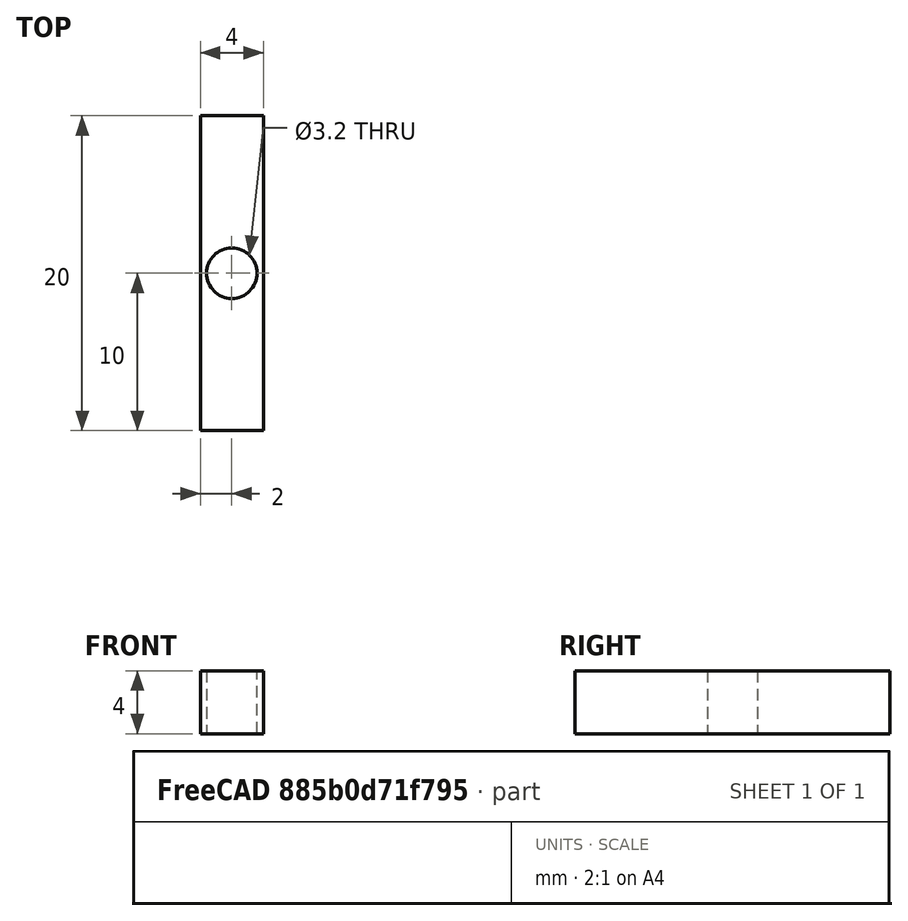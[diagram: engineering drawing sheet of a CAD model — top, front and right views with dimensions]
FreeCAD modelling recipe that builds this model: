
FCSTD DOCUMENT  (FreeCAD 0.18R14090 (Git))
Label: XEndStopClip3
License: All rights reserved
LicenseURL: http://en.wikipedia.org/wiki/All_rights_reserved
objects: Sketcher::SketchObject×1, PartDesign::Pad×1, PartDesign::Body×1, App::Part×1
note: 4 computed .brp shape members not serialized (recipe doc carries the construction recipe); baked Part::Feature solids carry a one-line shape summary decoded from their .brp

FEATURE [Sketcher::SketchObject] Sketch  label="BaseSketch"
  MapMode = 5
  Support = -> [XY_Plane001]
  sketch-geometry (8):
    g0: LineSegment StartX=0 StartY=0 StartZ=0 EndX=4 EndY=0 EndZ=0
    g1: LineSegment StartX=4 StartY=0 StartZ=0 EndX=4 EndY=20 EndZ=0
    g2: LineSegment StartX=4 StartY=20 StartZ=0 EndX=0 EndY=20 EndZ=0
    g3: LineSegment StartX=0 StartY=20 StartZ=0 EndX=0 EndY=0 EndZ=0
    g4: LineSegment [constr] StartX=4 StartY=20 StartZ=0 EndX=2 EndY=10 EndZ=0
    g5: LineSegment [constr] StartX=2 StartY=10 StartZ=0 EndX=0 EndY=0 EndZ=0
    g6: LineSegment [constr] StartX=2 StartY=10 StartZ=0 EndX=4 EndY=0 EndZ=0
    g7: Circle CenterX=2 CenterY=10 CenterZ=0 NormalX=0 NormalY=0 NormalZ=1 AngleXU=0 Radius=1.6
  constraints (20):
    c: Coincident(g0,g1)
    c: Coincident(g1,g2)
    c: Coincident(g2,g3)
    c: Coincident(g3,g0)
    c: Horizontal(g0)
    c: Horizontal(g2)
    c: Vertical(g1)
    c: Vertical(g3)
    c: Coincident(g0,g-1)
    c: Distance(g1) = 20
    c: Distance(g2) = 4
    c: Coincident(g4,g1)
    c: Coincident(g5,g4)
    c: Coincident(g5,g0)
    c: Coincident(g6,g4)
    c: Coincident(g6,g0)
    c: Equal(g4,g6)
    c: Equal(g6,g5)
    c: Coincident(g7,g4)
    c: Radius(g7) = 1.6
FEATURE [PartDesign::Pad] Pad  label="BasePad"
  Length = 4
  Length2 = 100
  Profile = -> Sketch
  Type = 0
FEATURE [PartDesign::Body] Body  label="PartBody"
  Group = -> [Sketch,Pad]
  Origin = -> Origin001
  Tip = -> Pad
FEATURE [App::Part] Part  label="XEndStopClipPart"
  Group = -> [Body]
  License = CC BY 3.0
  LicenseURL = http://creativecommons.org/licenses/by/3.0/
  Origin = -> Origin
